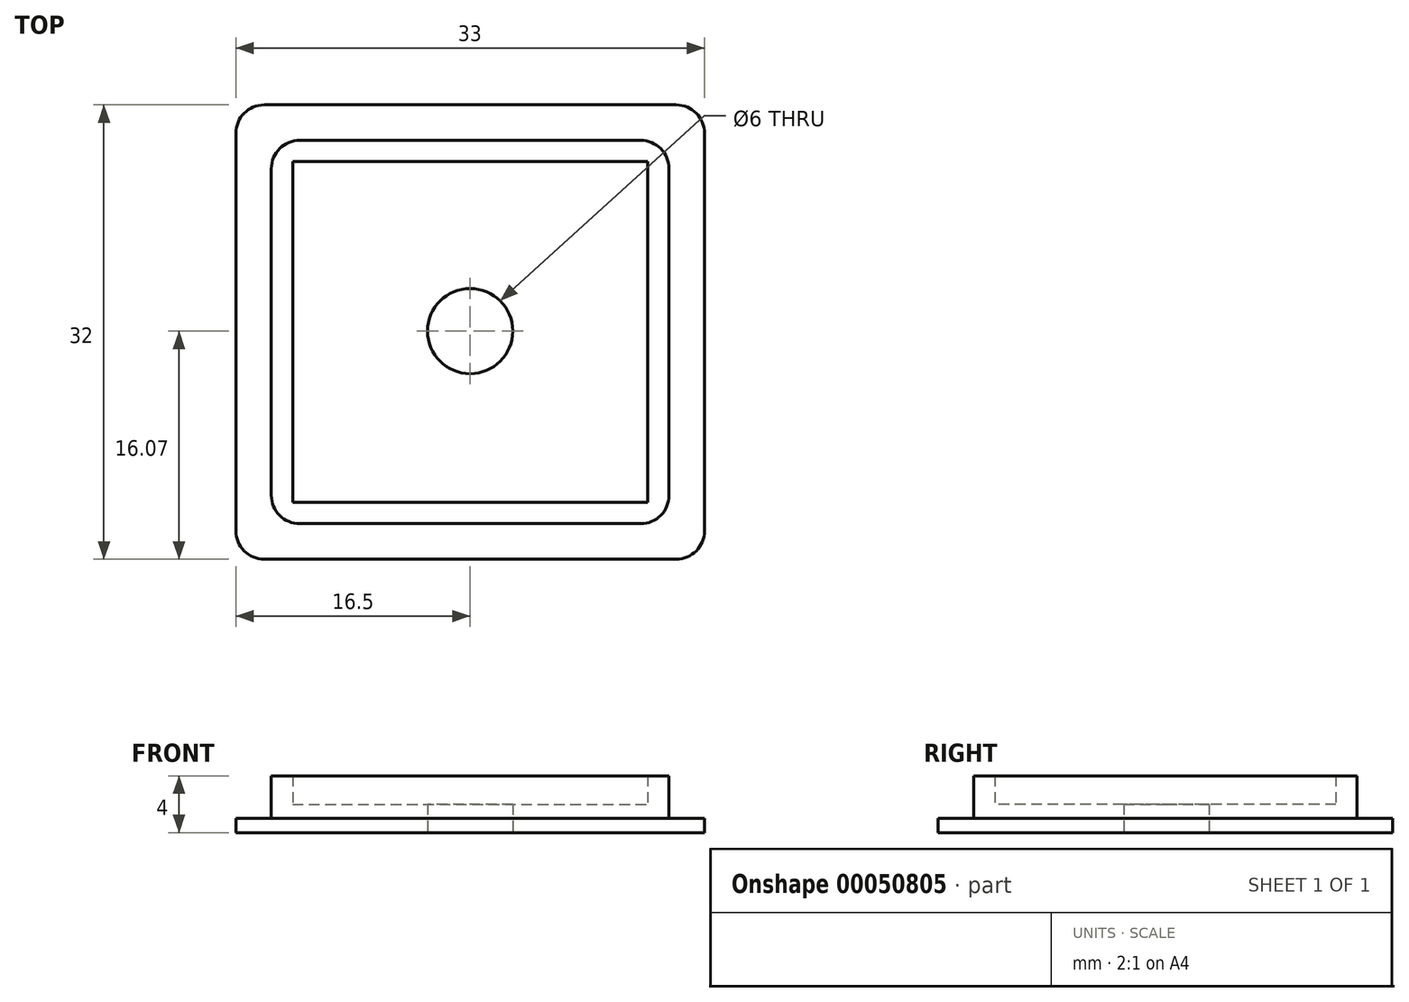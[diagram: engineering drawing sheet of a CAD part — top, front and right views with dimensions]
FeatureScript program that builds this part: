
annotation { "Feature Type Name" : "Feature", "Feature Type Description" : "" }
export const myFeature = defineFeature(function(context is Context, id is Id, definition is map)
    precondition{}
    {
        {
            var Q0;
            Q0=qCreatedBy(makeId("Top.planeOp"),FACE);
            var sketch = newSketch(context, id + "F0", { "sketchPlane" : qUnion([Q0])});
            skLineSegment(sketch, "E0.bottom", {"start": v(-12.5, 11.93) * mm, "end": v(12.5, 11.93) * mm});
            skLineSegment(sketch, "E0.top", {"start": v(-12.5, -12.07) * mm, "end": v(12.5, -12.07) * mm});
            skLineSegment(sketch, "E0.left", {"start": v(-12.5, 11.93) * mm, "end": v(-12.5, -12.07) * mm});
            skLineSegment(sketch, "E0.right", {"start": v(12.5, 11.93) * mm, "end": v(12.5, -12.07) * mm});
            skLineSegment(sketch, "E1.bottom", {"start": v(-12, 13.43) * mm, "end": v(12, 13.43) * mm});
            skLineSegment(sketch, "E1.top", {"start": v(-12, -13.57) * mm, "end": v(12, -13.57) * mm});
            skLineSegment(sketch, "E1.left", {"start": v(-14, 11.43) * mm, "end": v(-14, -11.57) * mm});
            skLineSegment(sketch, "E1.right", {"start": v(14, 11.43) * mm, "end": v(14, -11.57) * mm});
            skPoint(sketch, "E2.visualSharp", {"position": v(-14, 13.43) * mm});
            skArc(sketch, "E2.filletArc", {"start": v(-12, 13.43) * mm, "mid": v(-13.41, 12.85) * mm, "end": v(-14, 11.43) * mm});
            skPoint(sketch, "E3.visualSharp", {"position": v(-14, -13.57) * mm});
            skArc(sketch, "E3.filletArc", {"start": v(-14, -11.57) * mm, "mid": v(-13.41, -12.98) * mm, "end": v(-12, -13.57) * mm});
            skPoint(sketch, "E4.visualSharp", {"position": v(14, -13.57) * mm});
            skArc(sketch, "E4.filletArc", {"start": v(12, -13.57) * mm, "mid": v(13.41, -12.98) * mm, "end": v(14, -11.57) * mm});
            skPoint(sketch, "E5.visualSharp", {"position": v(14, 13.43) * mm});
            skArc(sketch, "E5.filletArc", {"start": v(14, 11.43) * mm, "mid": v(13.41, 12.85) * mm, "end": v(12, 13.43) * mm});
            skLineSegment(sketch, "E6.bottom", {"start": v(-14.5, 15.93) * mm, "end": v(14.5, 15.93) * mm});
            skLineSegment(sketch, "E6.top", {"start": v(-14.5, -16.07) * mm, "end": v(14.5, -16.07) * mm});
            skLineSegment(sketch, "E6.left", {"start": v(-16.5, 13.93) * mm, "end": v(-16.5, -14.07) * mm});
            skLineSegment(sketch, "E6.right", {"start": v(16.5, 13.93) * mm, "end": v(16.5, -14.07) * mm});
            skPoint(sketch, "E7.visualSharp", {"position": v(-16.5, 15.93) * mm});
            skArc(sketch, "E7.filletArc", {"start": v(-14.5, 15.93) * mm, "mid": v(-15.91, 15.35) * mm, "end": v(-16.5, 13.93) * mm});
            skPoint(sketch, "E8.visualSharp", {"position": v(-16.5, -16.07) * mm});
            skArc(sketch, "E8.filletArc", {"start": v(-16.5, -14.07) * mm, "mid": v(-15.91, -15.48) * mm, "end": v(-14.5, -16.07) * mm});
            skPoint(sketch, "E9.visualSharp", {"position": v(16.5, -16.07) * mm});
            skArc(sketch, "E9.filletArc", {"start": v(14.5, -16.07) * mm, "mid": v(15.91, -15.48) * mm, "end": v(16.5, -14.07) * mm});
            skPoint(sketch, "E10.visualSharp", {"position": v(16.5, 15.93) * mm});
            skArc(sketch, "E10.filletArc", {"start": v(16.5, 13.93) * mm, "mid": v(15.91, 15.35) * mm, "end": v(14.5, 15.93) * mm});
            skPoint(sketch, "E11.0.midPoint", {"position": v(-2.65, -1.56) * mm});
            skCircle(sketch, "E12", {"center": v(0, 0) * mm, "radius": 3 * mm});
            skSolve(sketch);
        }
        {
            var Q0;
            Q0=makeQuery(id+"F0.imprint","IMPRINT",FACE,{"disambiguationData":[TD([[makeQuery(id+"F0.imprint","IMPRINT",EDGE,{"derivedFrom":sQuery(id+"F0.wireOp",EDGE,"E0.bottom")}),-1.0]])]});
            extrude(context, id + "F1", {"entities" : qUnion([Q0]), "depth" : 2 * mm});
        }
        {
            var Q0;
            Q0=makeQuery(id+"F0.imprint","IMPRINT",FACE,{"disambiguationData":[TD([[makeQuery(id+"F0.imprint","IMPRINT",EDGE,{"derivedFrom":sQuery(id+"F0.wireOp",EDGE,"E0.bottom")}),1.0]])]});
            extrude(context, id + "F2", {"entities" : qUnion([Q0]), "operationType" : NewBodyOperationType.ADD, "depth" : 4 * mm});
        }
        {
            var Q0;
            Q0=makeQuery(id+"F0.imprint","IMPRINT",FACE,{"disambiguationData":[TD([[makeQuery(id+"F0.imprint","IMPRINT",EDGE,{"derivedFrom":sQuery(id+"F0.wireOp",EDGE,"E1.bottom")}),1.0]])]});
            extrude(context, id + "F3", {"entities" : qUnion([Q0]), "operationType" : NewBodyOperationType.ADD, "depth" : 1 * mm});
        }
    });
